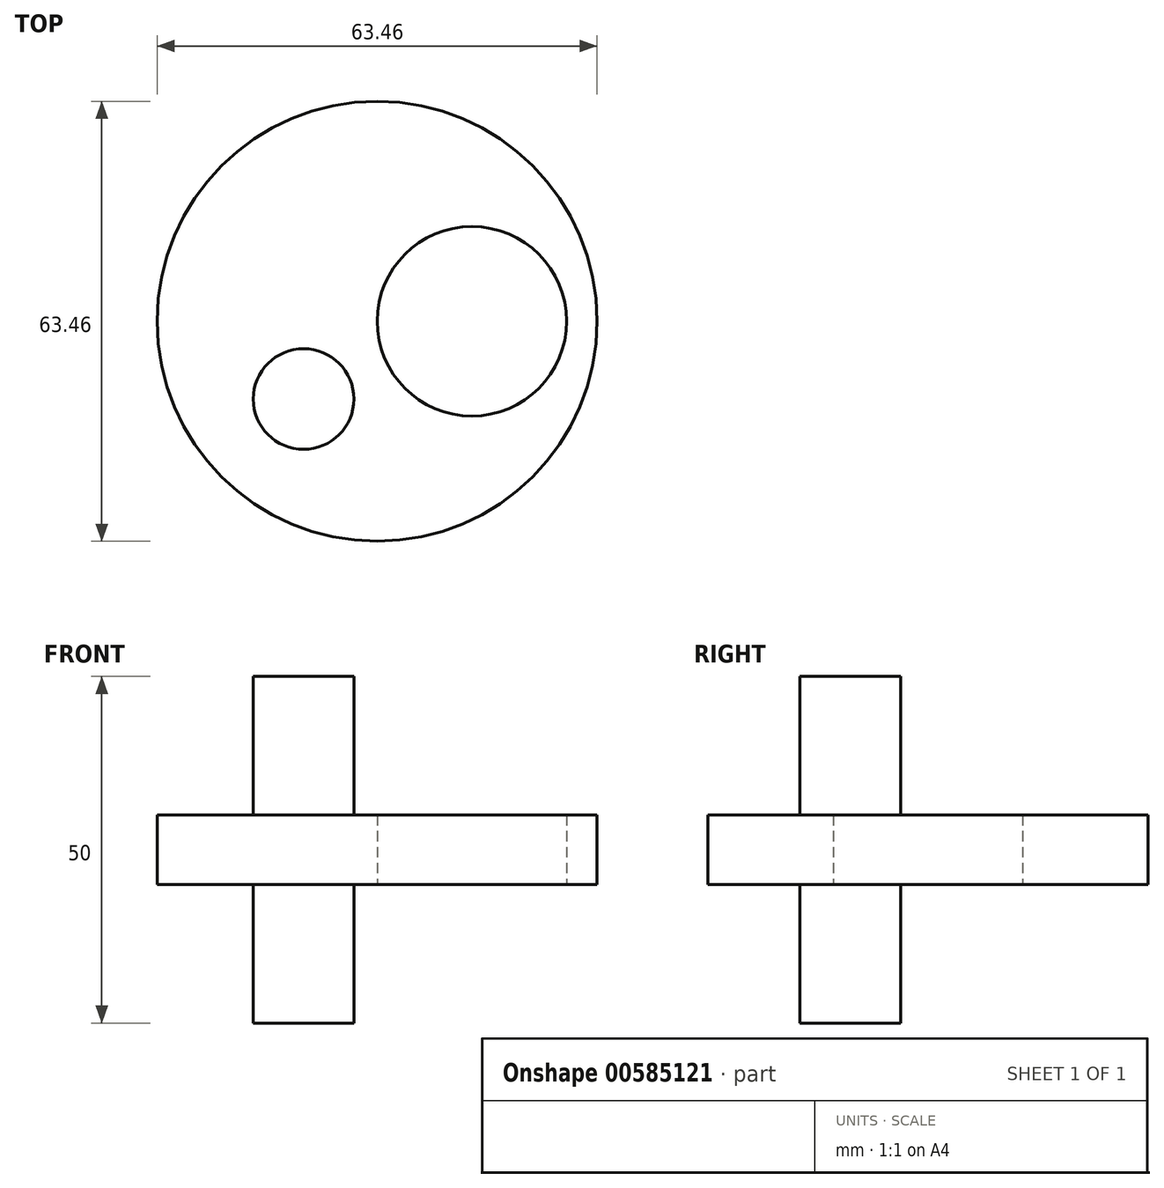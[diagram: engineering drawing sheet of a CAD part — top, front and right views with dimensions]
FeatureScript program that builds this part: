
annotation { "Feature Type Name" : "Feature", "Feature Type Description" : "" }
export const myFeature = defineFeature(function(context is Context, id is Id, definition is map)
    precondition{}
    {
        {
            var Q0;
            Q0=qCreatedBy(makeId("Top.planeOp"),FACE);
            var sketch = newSketch(context, id + "F0", { "sketchPlane" : qUnion([Q0])});
            skCircle(sketch, "E0", {"center": v(0, 0) * mm, "radius": 31.73 * mm});
            skCircle(sketch, "E1", {"center": v(13.67, 0) * mm, "radius": 13.67 * mm});
            skSolve(sketch);
        }
        {
            var Q0;
            Q0=makeQuery(id+"F0.imprint","IMPRINT",FACE,{"disambiguationData":[TD([[makeQuery(id+"F0.imprint","IMPRINT",EDGE,{"derivedFrom":sQuery(id+"F0.wireOp",EDGE,"E0")}),1.0]])]});
            extrude(context, id + "F1", {"entities" : qUnion([Q0]), "depth" : 5 * mm, "offsetDistance" : 25.4 * mm, "hasSecondDirection" : true, "secondDirectionOppositeDirection" : true, "secondDirectionDepth" : 5 * mm});
        }
        {
            var Q0;
            Q0=qCreatedBy(makeId("Top.planeOp"),FACE);
            var sketch = newSketch(context, id + "F2", { "sketchPlane" : qUnion([Q0])});
            skCircle(sketch, "E2", {"center": v(-10.62, -11.22) * mm, "radius": 7.26 * mm});
            skSolve(sketch);
        }
        {
            var Q0;
            Q0 = qSketchRegion(id + "F2", true);
            extrude(context, id + "F3", {"entities" : qUnion([Q0]), "operationType" : NewBodyOperationType.ADD, "depth" : 25 * mm, "offsetDistance" : 25.4 * mm, "hasSecondDirection" : true, "secondDirectionOppositeDirection" : true, "secondDirectionDepth" : 25 * mm});
        }
    });
